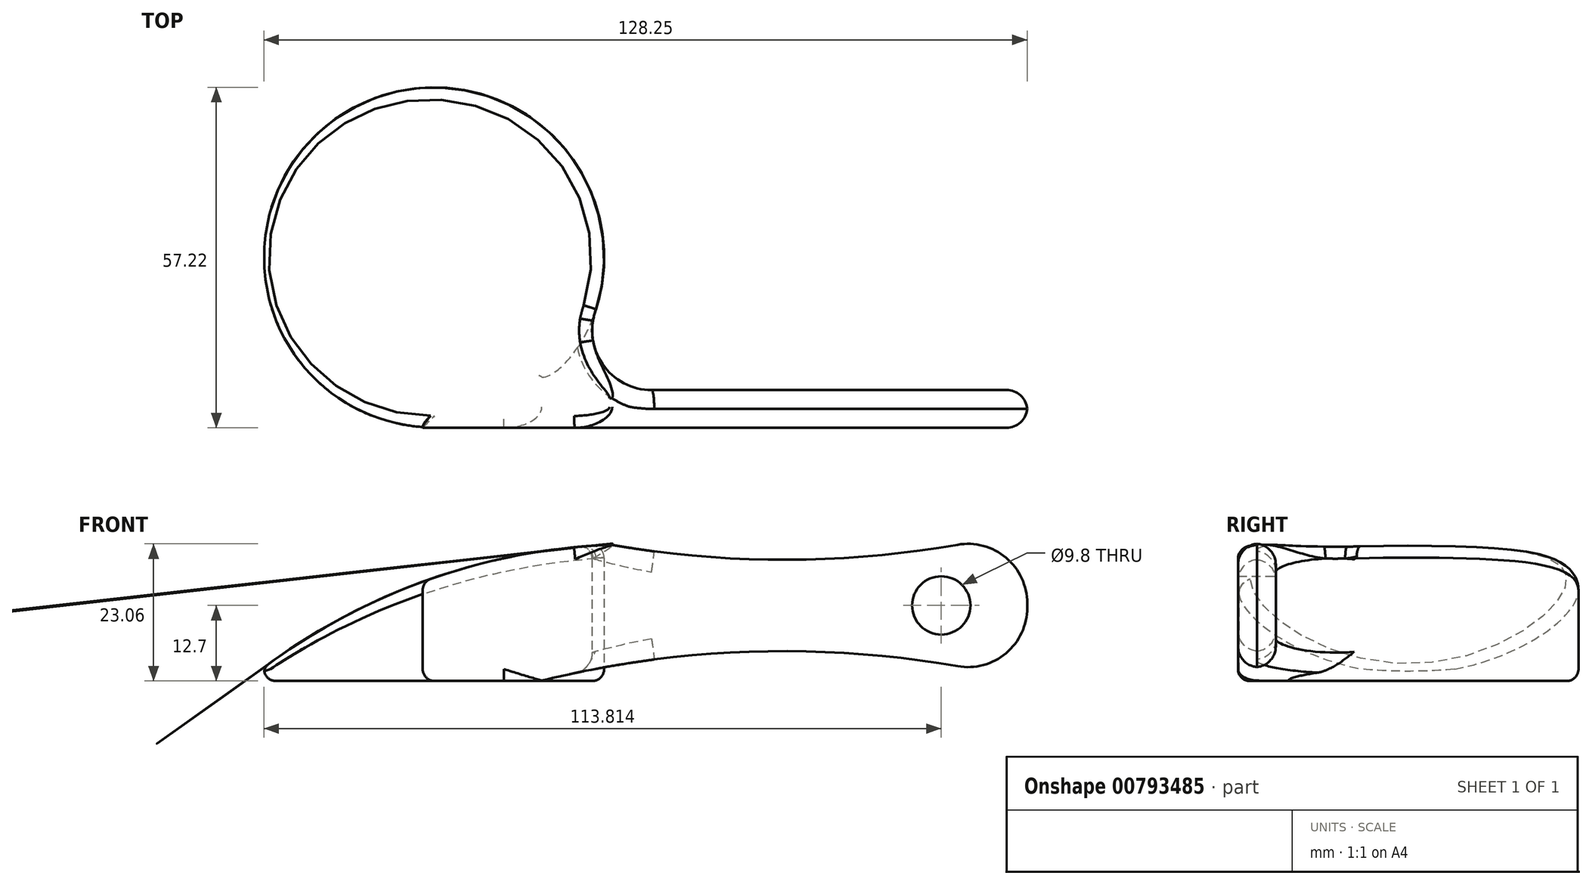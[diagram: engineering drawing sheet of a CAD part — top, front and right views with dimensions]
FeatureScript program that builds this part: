
annotation { "Feature Type Name" : "Feature", "Feature Type Description" : "" }
export const myFeature = defineFeature(function(context is Context, id is Id, definition is map)
    precondition{}
    {
        {
            var Q0;
            Q0=qCreatedBy(makeId("Top.planeOp"),FACE);
            var sketch = newSketch(context, id + "F0", { "sketchPlane" : qUnion([Q0])});
            skLineSegment(sketch, "E0.bottom", {"start": v(0, 0) * mm, "end": v(101.6, 0) * mm});
            skLineSegment(sketch, "E0.top", {"start": v(0, 6.35) * mm, "end": v(101.6, 6.35) * mm});
            skLineSegment(sketch, "E0.left", {"start": v(0, 0) * mm, "end": v(0, 6.35) * mm});
            skLineSegment(sketch, "E0.right", {"start": v(101.6, 0) * mm, "end": v(101.6, 6.35) * mm});
            skPoint(sketch, "E1", {"position": v(14.87, 3.18) * mm});
            skPoint(sketch, "E1.positionSnap0", {"position": v(0, 3.18) * mm});
            skCircle(sketch, "E2", {"center": v(1.9, 28.64) * mm, "radius": 28.58 * mm});
            skPoint(sketch, "E2.second.point", {"position": v(-26.42, 32.35) * mm});
            skPoint(sketch, "E2.third.point", {"position": v(-26.42, 24.9) * mm});
            skSolve(sketch);
        }
        {
            var Q0;
            {var subQ0=sQuery(id+"F0.wireOp",EDGE,"E0.left");Q0=makeQuery(id+"F0.imprint","IMPRINT",FACE,{"disambiguationData":[TD([[makeQuery(id+"F0.imprint","IMPRINT",EDGE,{"derivedFrom":subQ0}),1.0]])]});}
            var Q1;
            {var subQ0=sQuery(id+"F0.wireOp",EDGE,"E0.left");Q1=makeQuery(id+"F0.imprint","IMPRINT",FACE,{"disambiguationData":[TD([[makeQuery(id+"F0.imprint","IMPRINT",EDGE,{"derivedFrom":subQ0}),-1.0]])]});}
            var Q2;
            {var subQ0=sQuery(id+"F0.wireOp",EDGE,"E0.right");Q2=makeQuery(id+"F0.imprint","IMPRINT",FACE,{"disambiguationData":[TD([[makeQuery(id+"F0.imprint","IMPRINT",EDGE,{"derivedFrom":subQ0}),1.0]])]});}
            extrude(context, id + "F1", {"entities" : qUnion([Q0, Q1, Q2]), "depth" : 25.4 * mm, "offsetDistance" : 25 * mm});
        }
        {
            var Q0;
            Q0=makeQuery(id+"F1.opExtrude","SWEPT_FACE",FACE,{"disambiguationData":[OSD([sQuery(id+"F0.wireOp",EDGE,"E0.top")])]});
            var sketch = newSketch(context, id + "F2", { "sketchPlane" : qUnion([Q0])});
            skPoint(sketch, "E3", {"position": v(-87.14, 12.7) * mm});
            skArc(sketch, "E4", {"start": v(-101.6, 25.4) * mm, "mid": v(-60.7, 20.4) * mm, "end": v(-19.79, 25.4) * mm});
            skArc(sketch, "E5", {"start": v(-19.79, 0) * mm, "mid": v(-60.7, 5) * mm, "end": v(-101.6, 0) * mm});
            skSolve(sketch);
        }
        {
            var Q0;
            Q0=sQuery(id+"F2.wireOp",VERTEX,"E3");
            var Q1;
            Q1=makeQuery(id+"F1.opExtrude","SWEPT_BODY",BODY,{"disambiguationData":[OSD([sQuery(id+"F0.wireOp",EDGE,"E0.bottom"),sQuery(id+"F0.wireOp",EDGE,"E0.top"),sQuery(id+"F0.wireOp",EDGE,"E0.right"),sQuery(id+"F0.wireOp",EDGE,"E2")])]});
            hole(context, id + "F3", {"style" : HoleStyle.SIMPLE, "endStyle" : HoleEndStyle.THROUGH, "standardTappedOrClearance" : lookupTablePath({ "standard" : "ANSI", "fit" : "Close", "size" : "3/8", "type" : "Clearance" }), "standardBlindInLast" : lookupTablePath({ "fit" : "Close", "standard" : "ANSI", "size" : "3/8", "type" : "Clearance" }), "holeDiameter" : 9.8 * mm, "majorDiameter" : 5 * mm, "isTappedThrough" : true, "tappedDepth" : 12.7 * mm, "tapClearance" : 3, "locations" : qUnion([Q0]), "scope" : qUnion([Q1])});
        }
        {
            var Q0;
            Q0 = qSketchRegion(id + "F2", true);
            var Q1;
            Q1=makeQuery(id+"F2.imprint","IMPRINT",FACE,{"disambiguationData":[TD([[makeQuery(id+"F2.imprint","IMPRINT",EDGE,{"derivedFrom":sQuery(id+"F2.wireOp",EDGE,"E5")}),1.0]])]});
            var Q2;
            Q2=makeQuery(id+"F2.imprint","IMPRINT",FACE,{"disambiguationData":[TD([[makeQuery(id+"F2.imprint","IMPRINT",EDGE,{"derivedFrom":sQuery(id+"F2.wireOp",EDGE,"E4")}),1.0]])]});
            extrude(context, id + "F4", {"entities" : qUnion([Q0, Q1, Q2]), "operationType" : NewBodyOperationType.REMOVE, "oppositeDirection" : true, "depth" : 25 * mm, "offsetDistance" : 25 * mm});
        }
        {
            var Q0;
            {var subQ0=sQuery(id+"F0.wireOp",EDGE,"E0.right");Q0=makeQuery(id+"F4.boolean.opBoolean","MERGE",EDGE,{"derivedFrom":[makeQuery(id+"F1.opExtrude","CAP_EDGE",EDGE,{"disambiguationData":[OSD([subQ0])],"isStart":false}),makeQuery(id+"F4.opExtrude","SWEPT_EDGE",EDGE,{"disambiguationData":[OSD([sQuery(id+"F0.wireOp",EDGE,"E0.top"),subQ0,sQuery(id+"F2.wireOp",EDGE,"E4")])]})]});}
            var Q1;
            {var subQ0=sQuery(id+"F0.wireOp",EDGE,"E0.right");Q1=makeQuery(id+"F4.boolean.opBoolean","MERGE",EDGE,{"derivedFrom":[makeQuery(id+"F1.opExtrude","CAP_EDGE",EDGE,{"disambiguationData":[OSD([subQ0])],"isStart":true}),makeQuery(id+"F4.opExtrude","SWEPT_EDGE",EDGE,{"disambiguationData":[OSD([sQuery(id+"F0.wireOp",EDGE,"E0.top"),subQ0,sQuery(id+"F2.wireOp",EDGE,"E5")])]})]});}
            fillet(context, id + "F5", {"entities" : qUnion([Q0, Q1]), "radius" : 10 * mm, "tangentPropagation" : true, "allowEdgeOverflow" : false});
        }
        {
            var Q0;
            Q0=makeQuery(id+"F1.opExtrude","SWEPT_EDGE",EDGE,{"disambiguationData":[OSD([sQuery(id+"F0.wireOp",EDGE,"E0.top"),sQuery(id+"F0.wireOp",EDGE,"E2")])]});
            fillet(context, id + "F6", {"entities" : qUnion([Q0]), "radius" : 10 * mm, "tangentPropagation" : true, "allowEdgeOverflow" : false});
        }
        {
            var Q0;
            Q0=makeQuery(id+"F2.imprint","IMPRINT",FACE,{"disambiguationData":[TD([[makeQuery(id+"F2.imprint","IMPRINT",EDGE,{"derivedFrom":sQuery(id+"F2.wireOp",EDGE,"E4")}),1.0]])]});
            extrude(context, id + "F7", {"entities" : qUnion([Q0]), "operationType" : NewBodyOperationType.REMOVE, "depth" : 50 * mm, "offsetDistance" : 25 * mm});
        }
        {
            var Q0;
            Q0=qCreatedBy(makeId("Front.planeOp"),FACE);
            var sketch = newSketch(context, id + "F8", { "sketchPlane" : qUnion([Q0])});
            skLineSegment(sketch, "E6", {"start": v(33.27, 26.31) * mm, "end": v(-29.62, 26.31) * mm});
            skLineSegment(sketch, "E7", {"start": v(-29.62, 26.31) * mm, "end": v(-29.62, 0) * mm});
            skLineSegment(sketch, "E8", {"start": v(33.27, 26.31) * mm, "end": v(33.27, 22.95) * mm});
            skArc(sketch, "E9", {"start": v(33.27, 22.95) * mm, "mid": v(-0.07, 16.66) * mm, "end": v(-29.62, 0) * mm});
            skSolve(sketch);
        }
        {
            var Q0;
            Q0=makeQuery(id+"F8.imprint","IMPRINT",FACE,{"disambiguationData":[TD([[makeQuery(id+"F8.imprint","IMPRINT",EDGE,{"derivedFrom":sQuery(id+"F8.wireOp",EDGE,"E6")}),1.0]])]});
            extrude(context, id + "F9", {"entities" : qUnion([Q0]), "operationType" : NewBodyOperationType.REMOVE, "oppositeDirection" : true, "depth" : 58.42 * mm, "offsetDistance" : 25 * mm});
        }
        {
            var Q0;
            {var subQ0=sQuery(id+"F0.wireOp",EDGE,"E0.top");var subQ1=sQuery(id+"F0.wireOp",EDGE,"E0.right");Q0=makeQuery(id+"F5.opFillet","BLEND_EDGE",EDGE,{"blendedFrom":[makeQuery(id+"F4.boolean.opBoolean","MERGE",EDGE,{"derivedFrom":[makeQuery(id+"F1.opExtrude","CAP_EDGE",EDGE,{"disambiguationData":[OSD([subQ1])],"isStart":true}),makeQuery(id+"F4.opExtrude","SWEPT_EDGE",EDGE,{"disambiguationData":[OSD([subQ0,subQ1,sQuery(id+"F2.wireOp",EDGE,"E5")])]})]}),makeQuery(id+"F1.opExtrude","SWEPT_FACE",FACE,{"disambiguationData":[OSD([subQ0])]})],"blendedInto":[makeQuery(id+"F1.opExtrude","SWEPT_FACE",FACE,{"disambiguationData":[OSD([subQ0])]})]});}
            var Q1;
            Q1=makeQuery(id+"F4.boolean.opBoolean","COPY",EDGE,{"derivedFrom":makeQuery(id+"F4.opExtrude","CAP_EDGE",EDGE,{"disambiguationData":[OSD([sQuery(id+"F2.wireOp",EDGE,"E5")])],"isStart":true})});
            var Q2;
            Q2=makeQuery(id+"F4.boolean.opBoolean","COPY",EDGE,{"derivedFrom":makeQuery(id+"F4.opExtrude","CAP_EDGE",EDGE,{"disambiguationData":[OSD([sQuery(id+"F2.wireOp",EDGE,"E4")])],"isStart":true})});
            var Q3;
            {var subQ0=sQuery(id+"F0.wireOp",EDGE,"E0.top");var subQ1=sQuery(id+"F0.wireOp",EDGE,"E0.right");Q3=makeQuery(id+"F5.opFillet","BLEND_EDGE",EDGE,{"blendedFrom":[makeQuery(id+"F4.boolean.opBoolean","MERGE",EDGE,{"derivedFrom":[makeQuery(id+"F1.opExtrude","CAP_EDGE",EDGE,{"disambiguationData":[OSD([subQ1])],"isStart":false}),makeQuery(id+"F4.opExtrude","SWEPT_EDGE",EDGE,{"disambiguationData":[OSD([subQ0,subQ1,sQuery(id+"F2.wireOp",EDGE,"E4")])]})]}),makeQuery(id+"F1.opExtrude","SWEPT_FACE",FACE,{"disambiguationData":[OSD([subQ0])]})],"blendedInto":[makeQuery(id+"F1.opExtrude","SWEPT_FACE",FACE,{"disambiguationData":[OSD([subQ0])]})]});}
            var Q4;
            Q4=makeQuery(id+"F1.opExtrude","SWEPT_EDGE",EDGE,{"disambiguationData":[OSD([sQuery(id+"F0.wireOp",EDGE,"E0.top"),sQuery(id+"F0.wireOp",EDGE,"E0.right")])]});
            var Q5;
            Q5=makeQuery(id+"F4.boolean.opBoolean","INTERSECT",EDGE,{"derivedFrom":[makeQuery(id+"F1.opExtrude","SWEPT_FACE",FACE,{"disambiguationData":[OSD([sQuery(id+"F0.wireOp",EDGE,"E0.bottom")])]}),makeQuery(id+"F4.opExtrude","SWEPT_FACE",FACE,{"disambiguationData":[OSD([sQuery(id+"F2.wireOp",EDGE,"E5")])]})]});
            var Q6;
            Q6=makeQuery(id+"F4.boolean.opBoolean","INTERSECT",EDGE,{"derivedFrom":[makeQuery(id+"F1.opExtrude","SWEPT_FACE",FACE,{"disambiguationData":[OSD([sQuery(id+"F0.wireOp",EDGE,"E0.bottom")])]}),makeQuery(id+"F4.opExtrude","SWEPT_FACE",FACE,{"disambiguationData":[OSD([sQuery(id+"F2.wireOp",EDGE,"E4")])]})]});
            var Q7;
            {var subQ0=sQuery(id+"F0.wireOp",EDGE,"E0.right");Q7=makeQuery(id+"F5.opFillet","BLEND_EDGE",EDGE,{"blendedFrom":[makeQuery(id+"F4.boolean.opBoolean","MERGE",EDGE,{"derivedFrom":[makeQuery(id+"F1.opExtrude","CAP_EDGE",EDGE,{"disambiguationData":[OSD([subQ0])],"isStart":false}),makeQuery(id+"F4.opExtrude","SWEPT_EDGE",EDGE,{"disambiguationData":[OSD([sQuery(id+"F0.wireOp",EDGE,"E0.top"),subQ0,sQuery(id+"F2.wireOp",EDGE,"E4")])]})]}),makeQuery(id+"F1.opExtrude","SWEPT_FACE",FACE,{"disambiguationData":[OSD([sQuery(id+"F0.wireOp",EDGE,"E0.bottom")])]})],"blendedInto":[makeQuery(id+"F1.opExtrude","SWEPT_FACE",FACE,{"disambiguationData":[OSD([sQuery(id+"F0.wireOp",EDGE,"E0.bottom")])]})]});}
            var Q8;
            {var subQ0=sQuery(id+"F0.wireOp",EDGE,"E0.right");Q8=makeQuery(id+"F5.opFillet","BLEND_EDGE",EDGE,{"blendedFrom":[makeQuery(id+"F4.boolean.opBoolean","MERGE",EDGE,{"derivedFrom":[makeQuery(id+"F1.opExtrude","CAP_EDGE",EDGE,{"disambiguationData":[OSD([subQ0])],"isStart":true}),makeQuery(id+"F4.opExtrude","SWEPT_EDGE",EDGE,{"disambiguationData":[OSD([sQuery(id+"F0.wireOp",EDGE,"E0.top"),subQ0,sQuery(id+"F2.wireOp",EDGE,"E5")])]})]}),makeQuery(id+"F1.opExtrude","SWEPT_FACE",FACE,{"disambiguationData":[OSD([sQuery(id+"F0.wireOp",EDGE,"E0.bottom")])]})],"blendedInto":[makeQuery(id+"F1.opExtrude","SWEPT_FACE",FACE,{"disambiguationData":[OSD([sQuery(id+"F0.wireOp",EDGE,"E0.bottom")])]})]});}
            var Q9;
            Q9=makeQuery(id+"F1.opExtrude","SWEPT_EDGE",EDGE,{"disambiguationData":[OSD([sQuery(id+"F0.wireOp",EDGE,"E0.bottom"),sQuery(id+"F0.wireOp",EDGE,"E0.right")])]});
            fillet(context, id + "F10", {"entities" : qUnion([Q0, Q1, Q2, Q3, Q4, Q5, Q6, Q7, Q8, Q9]), "radius" : 3.5 * mm, "tangentPropagation" : true, "allowEdgeOverflow" : false});
        }
        {
            var Q0;
            Q0=makeQuery(id+"F1.opExtrude","CAP_FACE",FACE,{"disambiguationData":[OSD([sQuery(id+"F0.wireOp",EDGE,"E0.bottom"),sQuery(id+"F0.wireOp",EDGE,"E0.top"),sQuery(id+"F0.wireOp",EDGE,"E0.left"),sQuery(id+"F0.wireOp",EDGE,"E0.right"),sQuery(id+"F0.wireOp",EDGE,"E2")])],"isStart":true});
            var Q1;
            Q1=makeQuery(id+"F9.boolean.opBoolean","COPY",FACE,{"derivedFrom":makeQuery(id+"F9.opExtrude","SWEPT_FACE",FACE,{"disambiguationData":[OSD([sQuery(id+"F8.wireOp",EDGE,"E9")])]})});
            fillet(context, id + "F11", {"entities" : qUnion([Q0, Q1]), "radius" : 2 * mm, "tangentPropagation" : true, "allowEdgeOverflow" : false});
        }
    });
